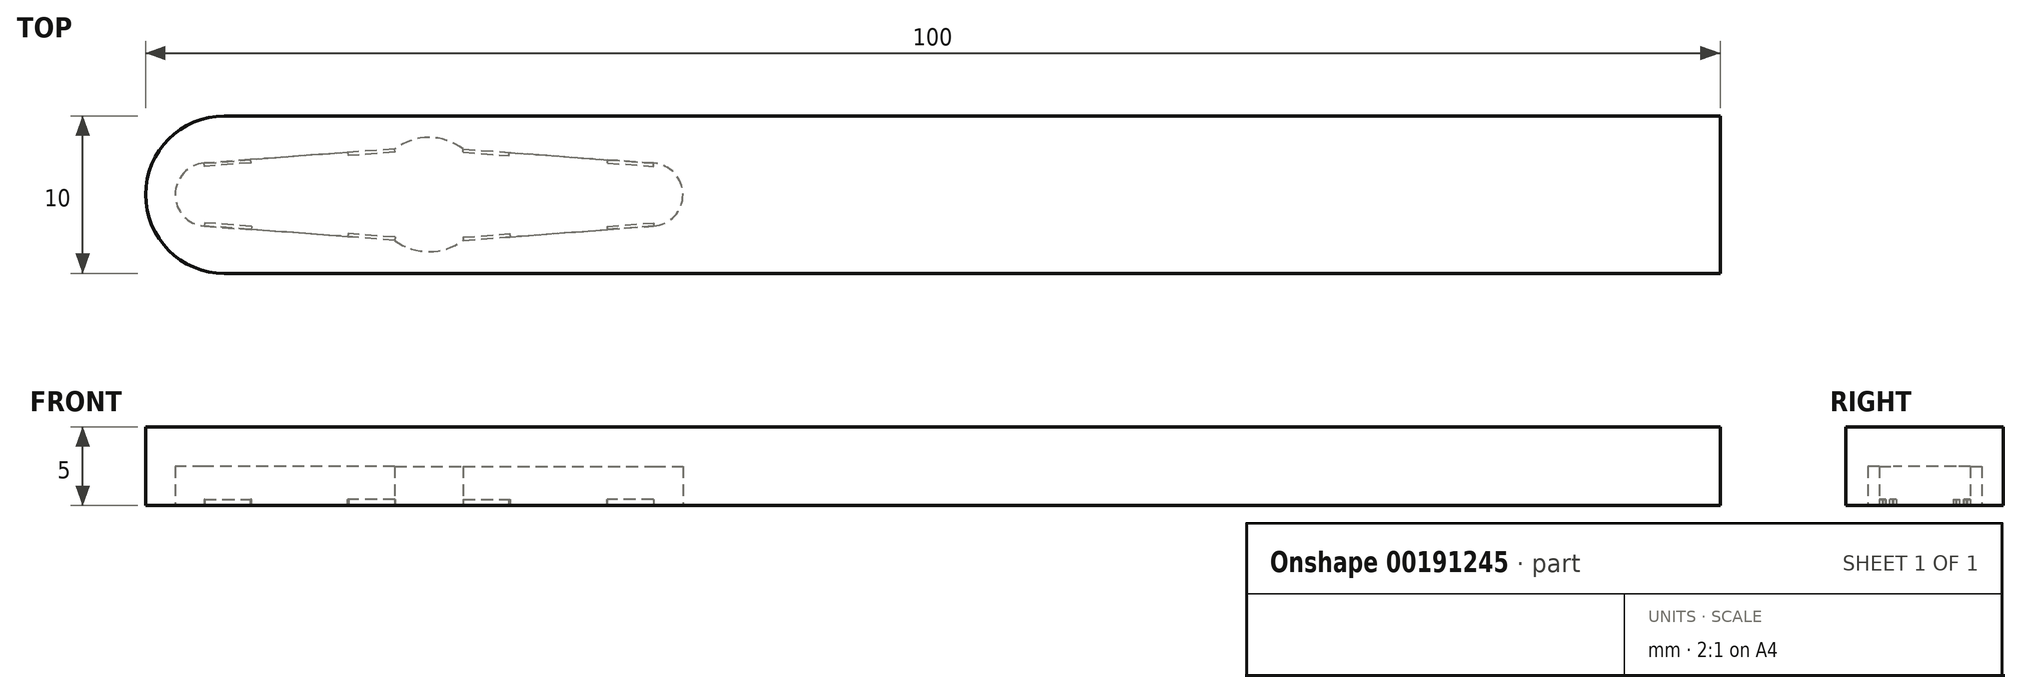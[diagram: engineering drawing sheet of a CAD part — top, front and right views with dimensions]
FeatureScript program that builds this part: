
annotation { "Feature Type Name" : "Feature", "Feature Type Description" : "" }
export const myFeature = defineFeature(function(context is Context, id is Id, definition is map)
    precondition{}
    {
        {
            var Q0;
            Q0=qCreatedBy(makeId("Top.planeOp"),FACE);
            var sketch = newSketch(context, id + "F0", { "sketchPlane" : qUnion([Q0])});
            skCircle(sketch, "E0", {"center": v(-14.13, 0) * mm, "radius": 2 * mm});
            skCircle(sketch, "E1", {"center": v(14.12, 0) * mm, "radius": 2 * mm});
            skCircle(sketch, "E2", {"center": v(0, 0) * mm, "radius": 3.62 * mm});
            skLineSegment(sketch, "E3", {"start": v(0, 3.06) * mm, "end": v(14.27, 2) * mm});
            skLineSegment(sketch, "E4", {"start": v(0, 3.06) * mm, "end": v(-14.27, 2) * mm});
            skLineSegment(sketch, "E5", {"start": v(0, -3.06) * mm, "end": v(14.27, -2) * mm});
            skLineSegment(sketch, "E6", {"start": v(0, -3.06) * mm, "end": v(-14.27, -2) * mm});
            skLineSegment(sketch, "E7", {"start": v(-2.17, -2.9) * mm, "end": v(2.17, -2.9) * mm, "construction": true});
            skSolve(sketch);
        }
        {
            var Q0;
            Q0=qCreatedBy(makeId("Top.planeOp"),FACE);
            var sketch = newSketch(context, id + "F1", { "sketchPlane" : qUnion([Q0])});
            skLineSegment(sketch, "E8.bottom", {"start": v(-18, 5) * mm, "end": v(82, 5) * mm});
            skLineSegment(sketch, "E8.top", {"start": v(-18, -5) * mm, "end": v(82, -5) * mm});
            skLineSegment(sketch, "E8.left", {"start": v(-18, 5) * mm, "end": v(-18, -5) * mm});
            skLineSegment(sketch, "E8.right", {"start": v(82, 5) * mm, "end": v(82, -5) * mm});
            skSolve(sketch);
        }
        {
            var Q0;
            Q0=makeQuery(id+"F1.imprint","IMPRINT",FACE,{"disambiguationData":[TD([[makeQuery(id+"F1.imprint","IMPRINT",EDGE,{"derivedFrom":sQuery(id+"F1.wireOp",EDGE,"E8.bottom")}),-1.0]])]});
            extrude(context, id + "F2", {"entities" : qUnion([Q0]), "depth" : 5 * mm});
        }
        {
            var Q0;
            Q0 = qSketchRegion(id + "F0", true);
            extrude(context, id + "F3", {"entities" : qUnion([Q0]), "operationType" : NewBodyOperationType.REMOVE, "depth" : 2.5 * mm});
        }
        {
            var Q0;
            Q0=makeQuery(id+"F2.opExtrude","SWEPT_EDGE",EDGE,{"disambiguationData":[OSD([sQuery(id+"F1.wireOp",EDGE,"E8.bottom"),sQuery(id+"F1.wireOp",EDGE,"E8.left")])]});
            fillet(context, id + "F4", {"entities" : qUnion([Q0]), "radius" : 5 * mm, "tangentPropagation" : true, "allowEdgeOverflow" : false});
        }
        {
            var Q0;
            Q0=makeQuery(id+"F2.opExtrude","SWEPT_EDGE",EDGE,{"disambiguationData":[OSD([sQuery(id+"F1.wireOp",EDGE,"E8.top"),sQuery(id+"F1.wireOp",EDGE,"E8.left")])]});
            fillet(context, id + "F5", {"entities" : qUnion([Q0]), "radius" : 5 * mm, "tangentPropagation" : true, "allowEdgeOverflow" : false});
        }
        {
            var Q0;
            Q0=makeQuery(id+"F3.boolean.opBoolean","COPY",FACE,{"derivedFrom":makeQuery(id+"F3.opExtrude","SWEPT_FACE",FACE,{"disambiguationData":[OSD([sQuery(id+"F0.wireOp",EDGE,"E6")])]})});
            var sketch = newSketch(context, id + "F6", { "sketchPlane" : qUnion([Q0])});
            skLineSegment(sketch, "E9.bottom", {"start": v(14.09, 0) * mm, "end": v(11.09, 0) * mm});
            skLineSegment(sketch, "E9.top", {"start": v(14.09, 0.4) * mm, "end": v(11.09, 0.4) * mm});
            skLineSegment(sketch, "E9.left", {"start": v(14.09, 0) * mm, "end": v(14.09, 0.4) * mm});
            skLineSegment(sketch, "E9.right", {"start": v(11.09, 0) * mm, "end": v(11.09, 0.4) * mm});
            skPoint(sketch, "E10.oppositeSnap0", {"position": v(12.59, 0.4) * mm});
            skLineSegment(sketch, "E10.bottom", {"start": v(1.95, 0) * mm, "end": v(4.95, 0) * mm});
            skLineSegment(sketch, "E10.top", {"start": v(1.95, 0.4) * mm, "end": v(4.95, 0.4) * mm});
            skLineSegment(sketch, "E10.left", {"start": v(1.95, 0) * mm, "end": v(1.95, 0.4) * mm});
            skLineSegment(sketch, "E10.right", {"start": v(4.95, 0) * mm, "end": v(4.95, 0.4) * mm});
            skSolve(sketch);
        }
        {
            var Q0;
            Q0=makeQuery(id+"F6.imprint","IMPRINT",FACE,{"disambiguationData":[TD([[makeQuery(id+"F6.imprint","IMPRINT",EDGE,{"derivedFrom":sQuery(id+"F6.wireOp",EDGE,"E9.bottom")}),1.0]])]});
            var Q1;
            Q1=makeQuery(id+"F6.imprint","IMPRINT",FACE,{"disambiguationData":[TD([[makeQuery(id+"F6.imprint","IMPRINT",EDGE,{"derivedFrom":sQuery(id+"F6.wireOp",EDGE,"E10.bottom")}),1.0]])]});
            extrude(context, id + "F7", {"entities" : qUnion([Q0, Q1]), "operationType" : NewBodyOperationType.ADD, "depth" : 0.2 * mm});
        }
        {
            var Q0;
            Q0=makeQuery(id+"F3.boolean.opBoolean","COPY",FACE,{"derivedFrom":makeQuery(id+"F3.opExtrude","SWEPT_FACE",FACE,{"disambiguationData":[OSD([sQuery(id+"F0.wireOp",EDGE,"E5")])]})});
            var sketch = newSketch(context, id + "F8", { "sketchPlane" : qUnion([Q0])});
            skLineSegment(sketch, "E11.bottom", {"start": v(-1.95, 0.4) * mm, "end": v(-4.92, 0.4) * mm});
            skLineSegment(sketch, "E11.top", {"start": v(-1.95, 0) * mm, "end": v(-4.92, 0) * mm});
            skLineSegment(sketch, "E11.left", {"start": v(-1.95, 0.4) * mm, "end": v(-1.95, 0) * mm});
            skLineSegment(sketch, "E11.right", {"start": v(-4.92, 0.4) * mm, "end": v(-4.92, 0) * mm});
            skLineSegment(sketch, "E12.bottom", {"start": v(-14.09, 0) * mm, "end": v(-11.12, 0) * mm});
            skLineSegment(sketch, "E12.top", {"start": v(-14.09, 0.4) * mm, "end": v(-11.12, 0.4) * mm});
            skLineSegment(sketch, "E12.left", {"start": v(-14.09, 0) * mm, "end": v(-14.09, 0.4) * mm});
            skLineSegment(sketch, "E12.right", {"start": v(-11.12, 0) * mm, "end": v(-11.12, 0.4) * mm});
            skSolve(sketch);
        }
        {
            var Q0;
            Q0=makeQuery(id+"F8.imprint","IMPRINT",FACE,{"disambiguationData":[TD([[makeQuery(id+"F8.imprint","IMPRINT",EDGE,{"derivedFrom":sQuery(id+"F8.wireOp",EDGE,"E11.bottom")}),1.0]])]});
            var Q1;
            Q1=makeQuery(id+"F8.imprint","IMPRINT",FACE,{"disambiguationData":[TD([[makeQuery(id+"F8.imprint","IMPRINT",EDGE,{"derivedFrom":sQuery(id+"F8.wireOp",EDGE,"E12.bottom")}),-1.0]])]});
            extrude(context, id + "F9", {"entities" : qUnion([Q0, Q1]), "operationType" : NewBodyOperationType.ADD, "depth" : 0.2 * mm});
        }
        {
            var Q0;
            Q0=makeQuery(id+"F3.boolean.opBoolean","COPY",FACE,{"derivedFrom":makeQuery(id+"F3.opExtrude","SWEPT_FACE",FACE,{"disambiguationData":[OSD([sQuery(id+"F0.wireOp",EDGE,"E4")])]})});
            var sketch = newSketch(context, id + "F10", { "sketchPlane" : qUnion([Q0])});
            skLineSegment(sketch, "E13.bottom", {"start": v(-1.95, 0.4) * mm, "end": v(-4.92, 0.4) * mm});
            skLineSegment(sketch, "E13.top", {"start": v(-1.95, 0) * mm, "end": v(-4.92, 0) * mm});
            skLineSegment(sketch, "E13.left", {"start": v(-1.95, 0.4) * mm, "end": v(-1.95, 0) * mm});
            skLineSegment(sketch, "E13.right", {"start": v(-4.92, 0.4) * mm, "end": v(-4.92, 0) * mm});
            skLineSegment(sketch, "E14.bottom", {"start": v(-14.09, 0) * mm, "end": v(-11.12, 0) * mm});
            skLineSegment(sketch, "E14.top", {"start": v(-14.09, 0.4) * mm, "end": v(-11.12, 0.4) * mm});
            skLineSegment(sketch, "E14.left", {"start": v(-14.09, 0) * mm, "end": v(-14.09, 0.4) * mm});
            skLineSegment(sketch, "E14.right", {"start": v(-11.12, 0) * mm, "end": v(-11.12, 0.4) * mm});
            skSolve(sketch);
        }
        {
            var Q0;
            Q0=makeQuery(id+"F10.imprint","IMPRINT",FACE,{"disambiguationData":[TD([[makeQuery(id+"F10.imprint","IMPRINT",EDGE,{"derivedFrom":sQuery(id+"F10.wireOp",EDGE,"E13.bottom")}),1.0]])]});
            var Q1;
            Q1=makeQuery(id+"F10.imprint","IMPRINT",FACE,{"disambiguationData":[TD([[makeQuery(id+"F10.imprint","IMPRINT",EDGE,{"derivedFrom":sQuery(id+"F10.wireOp",EDGE,"E14.bottom")}),-1.0]])]});
            extrude(context, id + "F11", {"entities" : qUnion([Q0, Q1]), "operationType" : NewBodyOperationType.ADD, "depth" : 0.2 * mm});
        }
        {
            var Q0;
            Q0=makeQuery(id+"F3.boolean.opBoolean","COPY",FACE,{"derivedFrom":makeQuery(id+"F3.opExtrude","SWEPT_FACE",FACE,{"disambiguationData":[OSD([sQuery(id+"F0.wireOp",EDGE,"E3")])]})});
            var sketch = newSketch(context, id + "F12", { "sketchPlane" : qUnion([Q0])});
            skLineSegment(sketch, "E15.bottom", {"start": v(1.95, 0) * mm, "end": v(4.89, 0) * mm});
            skLineSegment(sketch, "E15.top", {"start": v(1.95, 0.4) * mm, "end": v(4.89, 0.4) * mm});
            skLineSegment(sketch, "E15.left", {"start": v(1.95, 0) * mm, "end": v(1.95, 0.4) * mm});
            skLineSegment(sketch, "E15.right", {"start": v(4.89, 0) * mm, "end": v(4.89, 0.4) * mm});
            skLineSegment(sketch, "E16.bottom", {"start": v(14.09, 0) * mm, "end": v(11.15, 0) * mm});
            skLineSegment(sketch, "E16.top", {"start": v(14.09, 0.4) * mm, "end": v(11.15, 0.4) * mm});
            skLineSegment(sketch, "E16.left", {"start": v(14.09, 0) * mm, "end": v(14.09, 0.4) * mm});
            skLineSegment(sketch, "E16.right", {"start": v(11.15, 0) * mm, "end": v(11.15, 0.4) * mm});
            skSolve(sketch);
        }
        {
            var Q0;
            Q0=makeQuery(id+"F12.imprint","IMPRINT",FACE,{"disambiguationData":[TD([[makeQuery(id+"F12.imprint","IMPRINT",EDGE,{"derivedFrom":sQuery(id+"F12.wireOp",EDGE,"E16.bottom")}),1.0]])]});
            var Q1;
            Q1=makeQuery(id+"F12.imprint","IMPRINT",FACE,{"disambiguationData":[TD([[makeQuery(id+"F12.imprint","IMPRINT",EDGE,{"derivedFrom":sQuery(id+"F12.wireOp",EDGE,"E15.bottom")}),1.0]])]});
            extrude(context, id + "F13", {"entities" : qUnion([Q0, Q1]), "operationType" : NewBodyOperationType.ADD, "depth" : 0.2 * mm});
        }
    });
